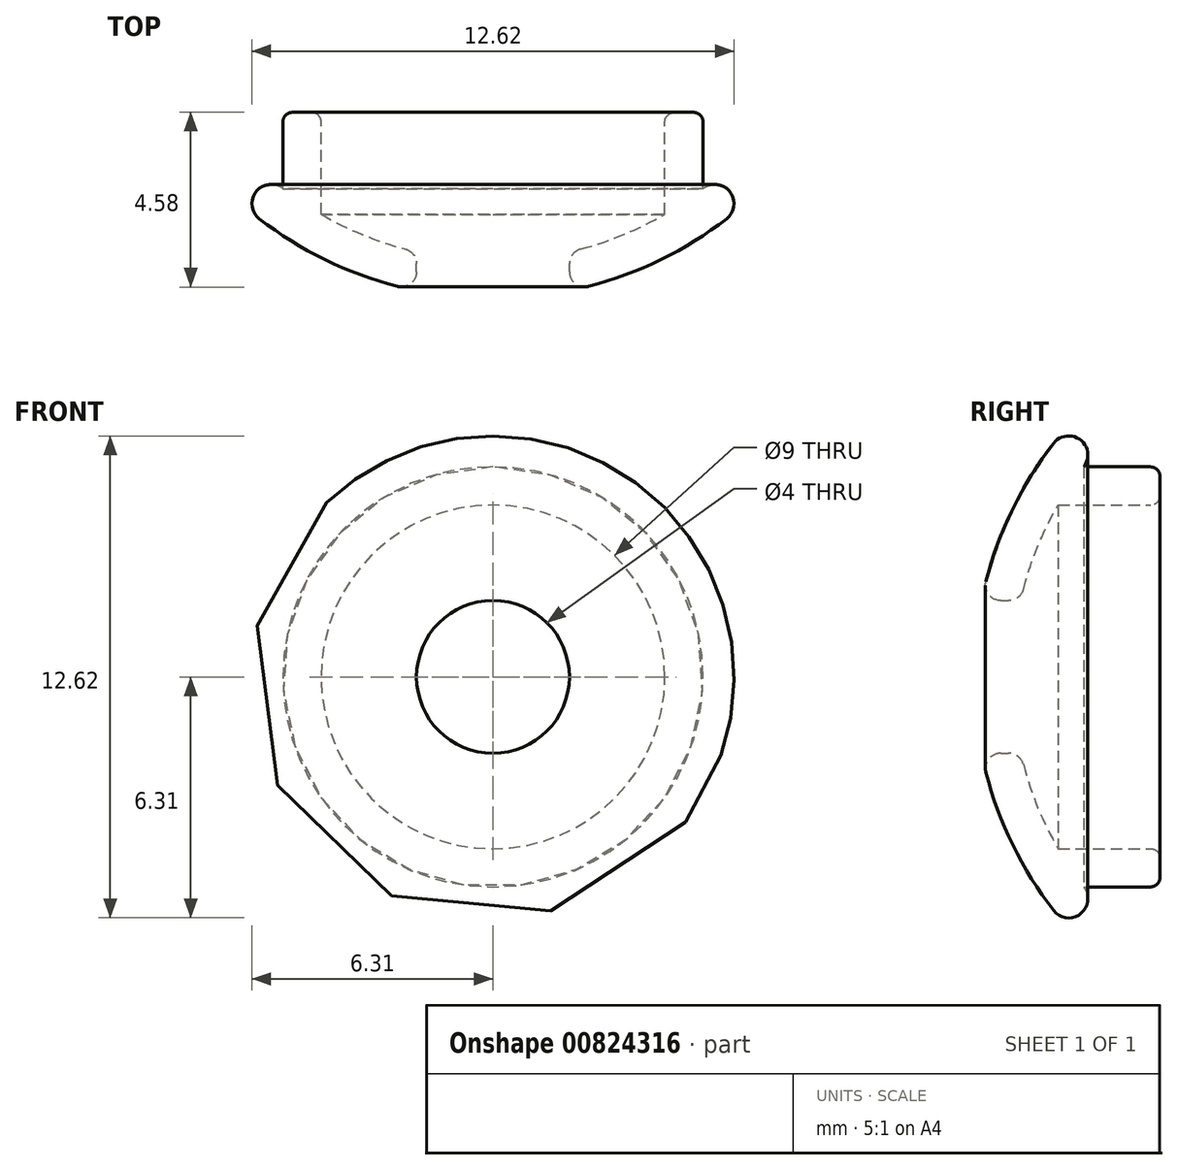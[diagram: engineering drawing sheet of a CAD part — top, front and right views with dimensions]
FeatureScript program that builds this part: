
annotation { "Feature Type Name" : "Feature", "Feature Type Description" : "" }
export const myFeature = defineFeature(function(context is Context, id is Id, definition is map)
    precondition{}
    {
        {
            var Q0;
            Q0=qCreatedBy(makeId("Right.planeOp"),FACE);
            var sketch = newSketch(context, id + "F0", { "sketchPlane" : qUnion([Q0])});
            skPoint(sketch, "E0.middle", {"position": v(0, 0) * mm});
            skLineSegment(sketch, "E1.top", {"start": v(-1.7, 2) * mm, "end": v(-1.49, 2) * mm});
            skArc(sketch, "E2", {"start": v(-0.31, 6.12) * mm, "mid": v(-1.38, 4.4) * mm, "end": v(-2.08, 2.5) * mm});
            skArc(sketch, "E3.0", {"start": v(0.48, 5.5) * mm, "mid": v(-0.47, 3.98) * mm, "end": v(-1.1, 2.3) * mm});
            skLineSegment(sketch, "E4", {"start": v(0.38, 6.21) * mm, "end": v(0.38, 6.21) * mm});
            skPoint(sketch, "E5.visualSharp", {"position": v(0, 6.5) * mm});
            skArc(sketch, "E5.filletArc", {"start": v(0.38, 6.21) * mm, "mid": v(0.02, 6.3) * mm, "end": v(-0.31, 6.12) * mm});
            skPoint(sketch, "E6.visualSharp", {"position": v(0.8, 5.9) * mm});
            skArc(sketch, "E6.filletArc", {"start": v(0.48, 5.5) * mm, "mid": v(0.58, 5.88) * mm, "end": v(0.38, 6.21) * mm});
            skLineSegment(sketch, "E7", {"start": v(2.23, 4.5) * mm, "end": v(-0.2, 4.5) * mm});
            skLineSegment(sketch, "E8.0", {"start": v(2.23, 5.5) * mm, "end": v(0.48, 5.5) * mm});
            skLineSegment(sketch, "E9", {"start": v(2.48, 5.25) * mm, "end": v(2.48, 4.75) * mm});
            skPoint(sketch, "E10.visualSharp", {"position": v(2.48, 5.5) * mm});
            skArc(sketch, "E10.filletArc", {"start": v(2.48, 5.25) * mm, "mid": v(2.4, 5.43) * mm, "end": v(2.23, 5.5) * mm});
            skPoint(sketch, "E11.visualSharp", {"position": v(2.48, 4.5) * mm});
            skArc(sketch, "E11.filletArc", {"start": v(2.23, 4.5) * mm, "mid": v(2.4, 4.57) * mm, "end": v(2.48, 4.75) * mm});
            skPoint(sketch, "E12.newPointB", {"position": v(-4.82, 2) * mm});
            skArc(sketch, "E12.filletArc", {"start": v(-2.08, 2.5) * mm, "mid": v(-2.01, 2.16) * mm, "end": v(-1.7, 2) * mm});
            skPoint(sketch, "E13.newPointA", {"position": v(4.82, 2) * mm});
            skArc(sketch, "E13.filletArc", {"start": v(-1.49, 2) * mm, "mid": v(-1.25, 2.08) * mm, "end": v(-1.1, 2.3) * mm});
            skLineSegment(sketch, "E14", {"start": v(0, 0) * mm, "end": v(-5.88, 0) * mm});
            skSolve(sketch);
        }
        {
            var Q0;
            Q0 = qSketchRegion(id + "F0", true);
            var Q1;
            Q1=sQuery(id+"F0.wireOp",EDGE,"E14");
            revolve(context, id + "F1", {"surfaceOperationType" : NewSurfaceOperationType.NEW, "entities" : qUnion([Q0]), "axis" : qUnion([Q1]), "revolveType" : RevolveType.SYMMETRIC, "angle" : 360 * degree});
        }
    });
